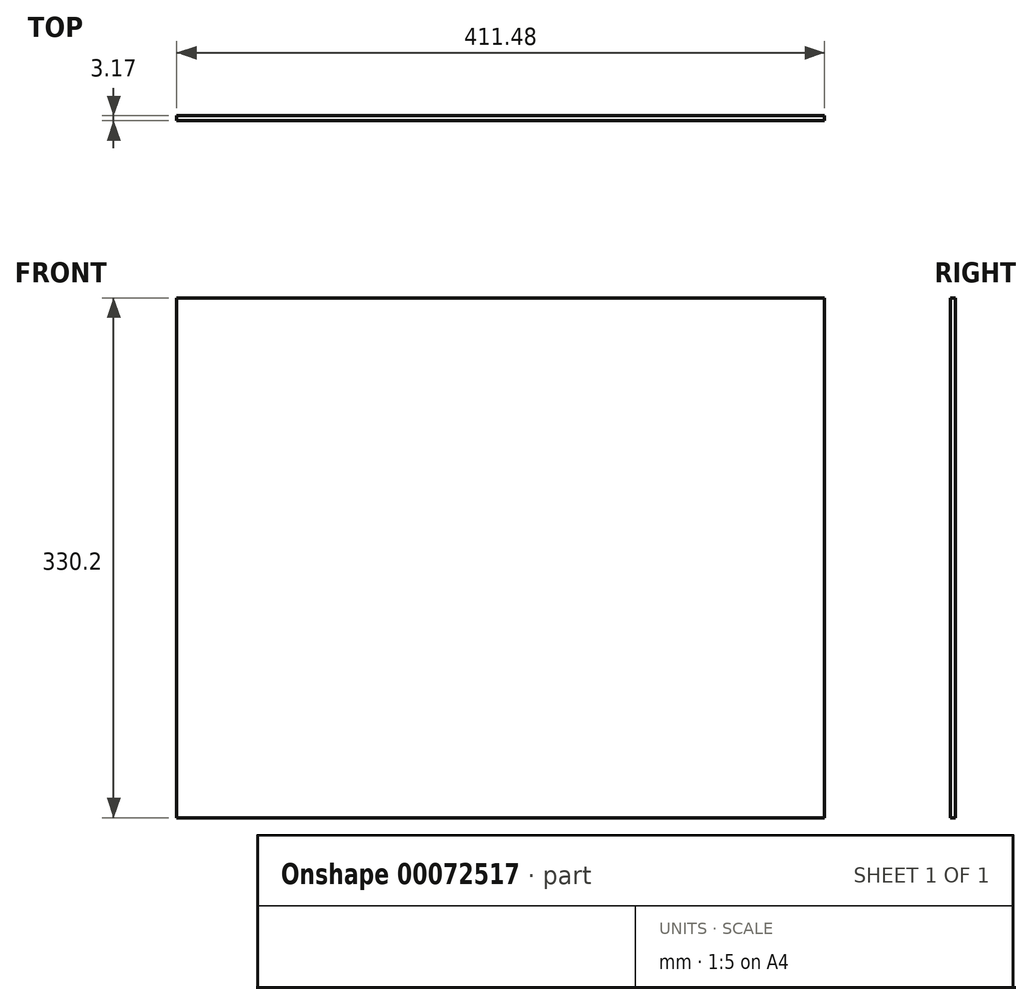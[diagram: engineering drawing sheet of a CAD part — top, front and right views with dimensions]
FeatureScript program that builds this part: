
annotation { "Feature Type Name" : "Feature", "Feature Type Description" : "" }
export const myFeature = defineFeature(function(context is Context, id is Id, definition is map)
    precondition{}
    {
        {
            var Q0;
            Q0=qCreatedBy(makeId("Front.planeOp"),FACE);
            var sketch = newSketch(context, id + "F0", { "sketchPlane" : qUnion([Q0])});
            skLineSegment(sketch, "E0.bottom", {"start": v(-144.93, 181.04) * mm, "end": v(266.55, 181.04) * mm});
            skLineSegment(sketch, "E0.top", {"start": v(-144.93, -149.16) * mm, "end": v(266.55, -149.16) * mm});
            skLineSegment(sketch, "E0.left", {"start": v(-144.93, 181.04) * mm, "end": v(-144.93, -149.16) * mm});
            skLineSegment(sketch, "E0.right", {"start": v(266.55, 181.04) * mm, "end": v(266.55, -149.16) * mm});
            skSolve(sketch);
        }
        {
            var Q0;
            Q0 = qSketchRegion(id + "F0", true);
            extrude(context, id + "F1", {"entities" : qUnion([Q0]), "depth" : 3.17 * mm});
        }
    });
